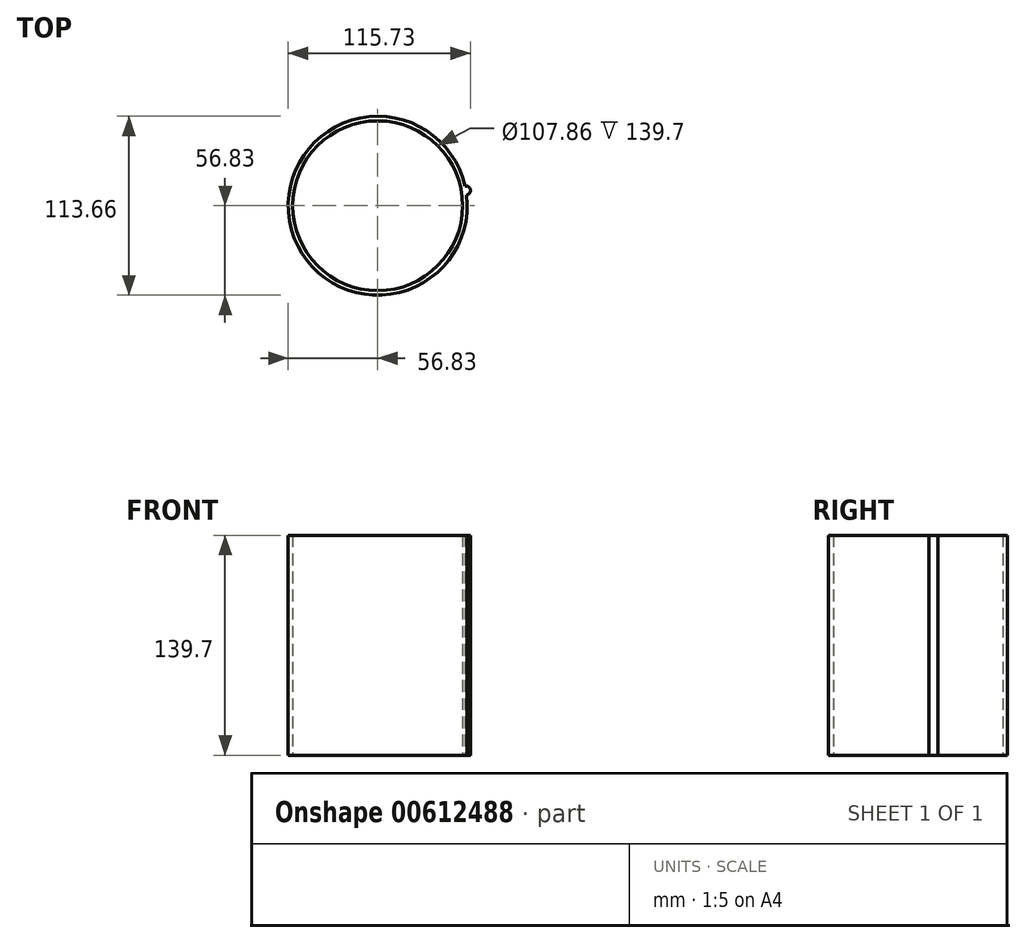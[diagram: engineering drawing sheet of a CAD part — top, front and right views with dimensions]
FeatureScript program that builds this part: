
annotation { "Feature Type Name" : "Feature", "Feature Type Description" : "" }
export const myFeature = defineFeature(function(context is Context, id is Id, definition is map)
    precondition{}
    {
        {
            var Q0;
            Q0=qCreatedBy(makeId("Top.planeOp"),FACE);
            var sketch = newSketch(context, id + "F0", { "sketchPlane" : qUnion([Q0])});
            skCircle(sketch, "E0", {"center": v(0, 0) * mm, "radius": 56.83 * mm});
            skCircle(sketch, "E1", {"center": v(0, 0) * mm, "radius": 53.93 * mm});
            skCircle(sketch, "E2", {"center": v(56, 9.72) * mm, "radius": 2.9 * mm});
            skSolve(sketch);
        }
        {
            var Q0;
            Q0 = qSketchRegion(id + "F0", true);
            extrude(context, id + "F1", {"entities" : qUnion([Q0]), "depth" : 25.4 * mm, "offsetDistance" : 25.4 * mm});
        }
        {
            var Q0;
            Q0=makeQuery(id+"F1.opExtrude","CAP_FACE",FACE,{"disambiguationData":[OSD([sQuery(id+"F0.wireOp",EDGE,"E0"),sQuery(id+"F0.wireOp",EDGE,"E1"),sQuery(id+"F0.wireOp",EDGE,"E2")])],"isStart":false});
            extrude(context, id + "F2", {"entities" : qUnion([Q0]), "operationType" : NewBodyOperationType.ADD, "depth" : 114.3 * mm, "offsetDistance" : 25.4 * mm});
        }
    });
